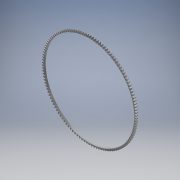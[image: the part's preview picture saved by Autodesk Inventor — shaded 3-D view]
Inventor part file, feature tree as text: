
AUTODESK INVENTOR PART (.ipt)
format: ipt  version: 2017 (Build 210142000, 142)  size: 651,264 bytes
history: native  units: mm (DEFAULTED — no unit token found)
features: plane x3, other x3, sketch x3, extrude x2
ambient origin geometry x8: Origin, YZ Plane, XZ Plane, XY Plane, X Axis, Y Axis, Z Axis, Center Point
bodies: Solid1 (feature_tree)
feature tree (11):
  extrude  "Extrusion1"  Depth=6.35mm TaperAngle=0.0deg
  plane  "Work Plane1"
  plane  "Work Plane2"
  plane  "Work Plane3"
  other  "Spur Gear"
  extrude  "Extrusion2"  Depth=76.2mm TaperAngle=0.0deg
  sketch  "Sketch1"  dims[d0=314.96mm d1=6.35mm d2=0.0mm]
  sketch  "Sketch2"  dims[d3=309.88mm d4=76.2mm d5=0.0mm]
  other  "Srf1"
  sketch  "Sketch3"  dims[d6=0.0mm d7=0.257508mm d9=0.0mm d14=0.0mm d15=173.99mm d16=0.0mm d17=0.0mm d18=0.0mm d19=173.99mm d20=302.26mm d21=25.4mm d22=0.0mm]
  other  "Pitch Diameter"
